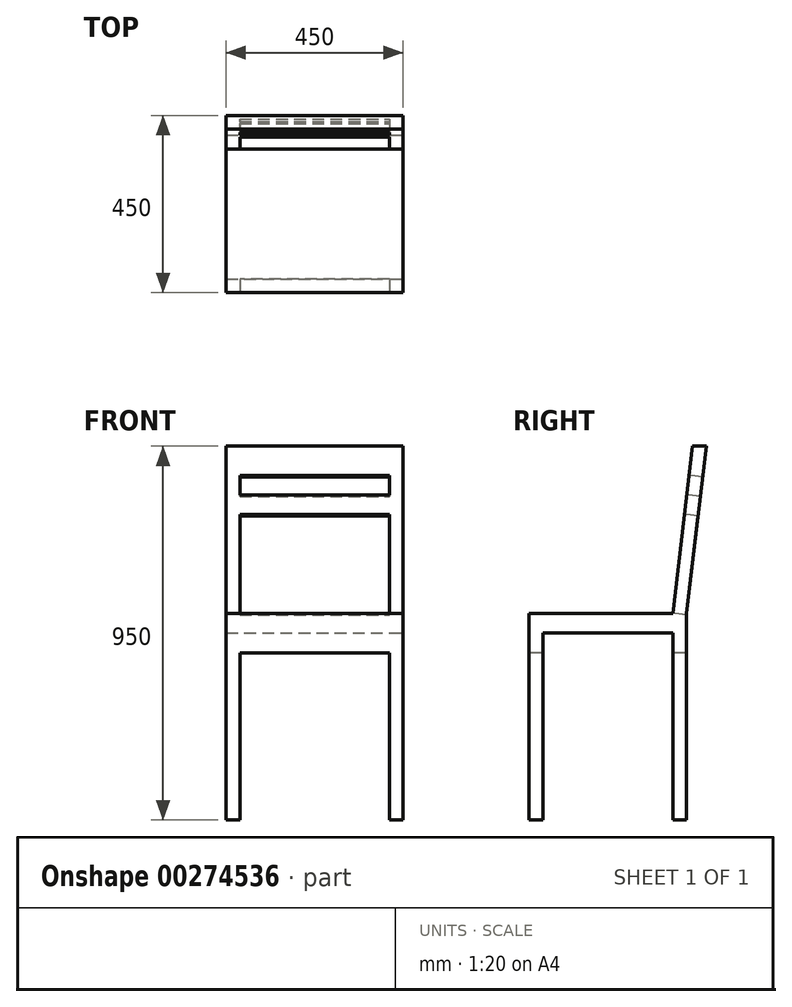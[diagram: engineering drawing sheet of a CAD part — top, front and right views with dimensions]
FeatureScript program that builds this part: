
annotation { "Feature Type Name" : "Feature", "Feature Type Description" : "" }
export const myFeature = defineFeature(function(context is Context, id is Id, definition is map)
    precondition{}
    {
        {
            var Q0;
            Q0=qCreatedBy(makeId("Top.planeOp"),FACE);
            var sketch = newSketch(context, id + "F0", { "sketchPlane" : qUnion([Q0])});
            skLineSegment(sketch, "E0.bottom", {"start": v(225, 225) * mm, "end": v(-225, 225) * mm});
            skLineSegment(sketch, "E0.top", {"start": v(225, -225) * mm, "end": v(-225, -225) * mm});
            skLineSegment(sketch, "E0.left", {"start": v(225, 225) * mm, "end": v(225, -225) * mm});
            skLineSegment(sketch, "E0.right", {"start": v(-225, 225) * mm, "end": v(-225, -225) * mm});
            skPoint(sketch, "E0.middle", {"position": v(0, 0) * mm});
            skSolve(sketch);
        }
        {
            var Q0;
            Q0=qSketchRegion(id+"F0",true);
            extrude(context, id + "F1", {"entities" : qUnion([Q0]), "depth" : 950 * mm});
        }
        {
            var Q0;
            Q0=makeQuery(id+"F1.opExtrude","SWEPT_FACE",FACE,{"disambiguationData":[OSD([sQuery(id+"F0.wireOp",EDGE,"E0.left")])]});
            var sketch = newSketch(context, id + "F2", { "sketchPlane" : qUnion([Q0])});
            skLineSegment(sketch, "E1.bottom", {"start": v(225, 525) * mm, "end": v(-225, 525) * mm});
            skLineSegment(sketch, "E1.top", {"start": v(225, 475) * mm, "end": v(-225, 475) * mm});
            skLineSegment(sketch, "E1.left", {"start": v(225, 525) * mm, "end": v(225, 475) * mm});
            skLineSegment(sketch, "E1.right", {"start": v(-225, 525) * mm, "end": v(-225, 475) * mm});
            skLineSegment(sketch, "E2", {"start": v(225, 950) * mm, "end": v(175, 525) * mm});
            skLineSegment(sketch, "E3", {"start": v(190, 950) * mm, "end": v(140, 525) * mm});
            skLineSegment(sketch, "E4", {"start": v(175, 525) * mm, "end": v(175, 0) * mm});
            skLineSegment(sketch, "E5", {"start": v(140, 525) * mm, "end": v(140, 0) * mm});
            skLineSegment(sketch, "E6.bottom", {"start": v(-225, 0) * mm, "end": v(-190, 0) * mm});
            skLineSegment(sketch, "E6.top", {"start": v(-225, 475) * mm, "end": v(-190, 475) * mm});
            skLineSegment(sketch, "E6.left", {"start": v(-225, 0) * mm, "end": v(-225, 475) * mm});
            skLineSegment(sketch, "E6.right", {"start": v(-190, 0) * mm, "end": v(-190, 475) * mm});
            skSolve(sketch);
        }
        {
            var Q0;
            {var subQ0=sQuery(id+"F2.wireOp",EDGE,"E6.right");Q0=makeQuery(id+"F2.imprint","IMPRINT",FACE,{"disambiguationData":[TD([[makeQuery(id+"F2.imprint","IMPRINT",EDGE,{"derivedFrom":subQ0}),-1.0]])]});}
            var Q1;
            {var subQ4=sQuery(id+"F2.wireOp",EDGE,"E3");Q1=makeQuery(id+"F2.imprint","IMPRINT",FACE,{"disambiguationData":[TD([[makeQuery(id+"F2.imprint","IMPRINT",EDGE,{"derivedFrom":subQ4}),-1.0]])]});}
            var Q2;
            {var subQ1=sQuery(id+"F0.wireOp",EDGE,"E0.left");var subQ4=sQuery(id+"F2.wireOp",EDGE,"E4");var subQ6=makeQuery(id+"F1.opExtrude","CAP_EDGE",EDGE,{"disambiguationData":[OSD([subQ1])],"isStart":true});var subQ7=makeQuery(id+"F2.imprint","INTERSECT",VERTEX,{"derivedFrom":[subQ6,subQ4]});Q2=makeQuery(id+"F2.imprint","IMPRINT",FACE,{"disambiguationData":[TD([[makeQuery(id+"F2.imprint","IMPRINT",EDGE,{"disambiguationData":[TD([[subQ7,1.0]])],"derivedFrom":subQ4}),1.0]])]});}
            var Q3;
            {var subQ0=sQuery(id+"F2.wireOp",EDGE,"E1.left");Q3=makeQuery(id+"F2.imprint","IMPRINT",FACE,{"disambiguationData":[TD([[makeQuery(id+"F2.imprint","IMPRINT",EDGE,{"derivedFrom":subQ0}),-1.0]])]});}
            var Q4;
            {var subQ4=sQuery(id+"F2.wireOp",EDGE,"E2");Q4=makeQuery(id+"F2.imprint","IMPRINT",FACE,{"disambiguationData":[TD([[makeQuery(id+"F2.imprint","IMPRINT",EDGE,{"derivedFrom":subQ4}),1.0]])]});}
            extrude(context, id + "F3", {"entities" : qUnion([Q0, Q1, Q2, Q3, Q4]), "operationType" : NewBodyOperationType.REMOVE, "endBound" : BoundingType.THROUGH_ALL, "oppositeDirection" : true, "depth" : 25 * mm});
        }
        {
            var Q0;
            Q0=makeQuery(id+"F1.opExtrude","SWEPT_FACE",FACE,{"disambiguationData":[OSD([sQuery(id+"F0.wireOp",EDGE,"E0.top")])]});
            var sketch = newSketch(context, id + "F4", { "sketchPlane" : qUnion([Q0])});
            skLineSegment(sketch, "E7", {"start": v(-190, 0) * mm, "end": v(-190, 425) * mm});
            skLineSegment(sketch, "E8", {"start": v(-190, 425) * mm, "end": v(190, 425) * mm});
            skLineSegment(sketch, "E9", {"start": v(190, 425) * mm, "end": v(190, 0) * mm});
            skSolve(sketch);
        }
        {
            var Q0;
            Q0 = qSketchRegion(id + "F4", true);
            var Q1;
            {var subQ0=sQuery(id+"F4.wireOp",EDGE,"E7");Q1=makeQuery(id+"F4.imprint","IMPRINT",FACE,{"disambiguationData":[TD([[makeQuery(id+"F4.imprint","IMPRINT",EDGE,{"derivedFrom":subQ0}),-1.0]])]});}
            extrude(context, id + "F5", {"entities" : qUnion([Q0, Q1]), "operationType" : NewBodyOperationType.REMOVE, "endBound" : BoundingType.THROUGH_ALL, "oppositeDirection" : true, "depth" : 25 * mm});
        }
        {
            var Q0;
            Q0=makeQuery(id+"F3.boolean.opBoolean","COPY",FACE,{"derivedFrom":makeQuery(id+"F3.opExtrude","SWEPT_FACE",FACE,{"disambiguationData":[OSD([sQuery(id+"F2.wireOp",EDGE,"E3")])]})});
            var sketch = newSketch(context, id + "F6", { "sketchPlane" : qUnion([Q0])});
            skLineSegment(sketch, "E10", {"start": v(-190, 537.76) * mm, "end": v(-190, 890.7) * mm});
            skLineSegment(sketch, "E11", {"start": v(-190, 890.7) * mm, "end": v(190, 890.7) * mm});
            skLineSegment(sketch, "E12", {"start": v(190, 890.7) * mm, "end": v(190, 537.76) * mm});
            skLineSegment(sketch, "E13", {"start": v(-190, 840.7) * mm, "end": v(190, 840.7) * mm});
            skLineSegment(sketch, "E14", {"start": v(-190, 790.7) * mm, "end": v(190, 790.7) * mm});
            skSolve(sketch);
        }
        {
            var Q0;
            {var subQ0=sQuery(id+"F6.wireOp",EDGE,"E11");Q0=makeQuery(id+"F6.imprint","IMPRINT",FACE,{"disambiguationData":[TD([[makeQuery(id+"F6.imprint","IMPRINT",EDGE,{"derivedFrom":subQ0}),-1.0]])]});}
            var Q1;
            {var subQ3=sQuery(id+"F6.wireOp",EDGE,"E14");Q1=makeQuery(id+"F6.imprint","IMPRINT",FACE,{"disambiguationData":[TD([[makeQuery(id+"F6.imprint","IMPRINT",EDGE,{"derivedFrom":subQ3}),-1.0]])]});}
            extrude(context, id + "F7", {"entities" : qUnion([Q0, Q1]), "operationType" : NewBodyOperationType.REMOVE, "endBound" : BoundingType.THROUGH_ALL, "oppositeDirection" : true, "depth" : 25 * mm});
        }
    });
